# Revit family: NBS_Allermuir_DmstcChrs_Mote-en-us_Sofa
name_source: partatom
category: Furniture
revit_build: Autodesk Revit 2016 (Build: 20151007_0715(x64)
units: mm (PartAtom-declared; Revit-internal decimal feet)

## family parameters
Always vertical = Yes
Cut with Voids When Loaded = No
Room Calculation Point = No
Shared = No
Work Plane-Based = No

## types (17) — shared parameters
AssetType = Moveable
Category = Pr_40_50_12_22:Dining chairs
DurationUnit = year
ExpectedLife = 10
FrameColourOptions = Flint grey, mineral sand, mellow yellow, orange crush
FrameMountingMaterial = NBS_Concept
FramesColour = Black
FramesFinish = Powder coat
FramesMaterial = Aluminum
IfcExportAs = IfcFurnitureType
IfcExportType = SOFA
IsBuiltIn = No
ManufacturerName = Allermuir
ManufacturerURL = http://www.thesenatorgroup.com
NBSCertification = www.nationalbimlibrary.com/cert/or0n0v02
NBSDescription = Domestic chairs
NBSReference = 45-35-20/365
OmniClassCode = 22-12 52 23
OmniClassTitle = Office Seating
OmniClassVersion = Table 22 2012-05-16
ProductInformation = http://www.thesenatorgroup.com
ScreenFinishMaterial = NBS_Concept
SeatArmRestHeight = 24 "
SeatEndRestOffset = 3 "
SeatFrameMaterial = NBS_Concept
SeatFrameWidth = 2 "
SeatLegOffset = 6 "
SeatPowerSupplyMaterial = NBS_Concept
SeatScreenHeight = 52 "
SeatingArmRestMaterial = NBS_Concept
SeatingHeight = 19 "
SeatingSeatMaterial = NBS_Concept
SeatsAndBacksFinish = Two-tone upholstery
SeatsAndBacksMaterial = Upholstered
ShelfMaterial = NBS_Concept
SingleSeatWidth = 39 "
Status = UNSET
ThreeSeatWidth = 87 "
TwoSeatWidth = 63 "
Uniclass2015Code = Pr_40_50_12_22
Uniclass2015Title = Dining chairs
Uniclass2015Version = Products v1.9
Version = 1
WarrantyDescription = Allermuir warrant that its manufactured products are free from manufacturing defects in materials or workmanship for a period of ten years
WarrantyDurationParts = 10
WarrantyDurationUnit = year
zero-valued in all types: HighestSeatingHeight, LowestSeatingHeight

## per-type parameters (varying)
| type | BIMObjectName | Description | Features | HasLeftSideScreen | HasRightSideScreen | HasScreens | HasShelf | IsSingleSeat | IsThreeSeat | IsTwoSeat | LeftSeatPositionOffset | ModelReference | Name | NominalDepth | NominalHeight | NominalLength | NominalWidth | OptionalAccessories | RightSeatPositionWidth | SeatOverallWidth | ShowMultipleSeat | Size |
| MTESF01 | NBS_Allermuir_DomesticChairs_Mote_MTESF01-US | Single seat sofa | Fully upholstered, cast aluminum legs and aluminum perimeter frame finished in black powder coat, plastic glides with leveling adjustment, two-tone upholstery, cast aluminum frame available in flint gray, mineral sand, mellow yellow or orange crush, end arms, 1 x front facing, frame integrated power unit - 2 x powered USB and 1 x power outlet, 1 x rear facing, frame integrated power unit - 2 x powered USB and 1 x power outlet | No | No | No | No | Yes | No | No | 0 " | Mote sofa | DomesticChairs_Mote_MTE-SF01_Allermuir | 39 " | 33 " | 29 " | 39 " | 1 x front facing frame intergrated power unit with 2 x powered USB and 1 x power socket, 1 x rear facing frame intergrated power unit with 2 x powered USB and 1 x power socket, End arms | 16 " | 39 " | No | 28.75 x 39.25 x 32.75" |
| MTESF02 | NBS_Allermuir_DomesticChairs_Mote_MTESF02-US | Two seat sofa | Fully upholstered, cast aluminum legs and aluminum perimeter frame finished in black powder coat, plastic glides with leveling adjustment, end arms, single arm mid, two-tone upholstery, Cast aluminum frame available in flint gray, mineral sand, mellow yellow or orange crush, 1 x front facing, frame integrated power unit - 2 x powered USB and 1 x power outlet, 1 x rear facing, frame integrated power unit - 2 x powered USBand 1 x power outlet | No | No | No | No | No | No | Yes | 0 " | Mote sofa | DomesticChairs_Mote_MTE-SF02_Allermuir | 63 " | 33 " | 29 " | 63 " | 1 x front facing frame intergrated power unit with 2 x powered USB and 1 x power socket, 1x rear facing frame intergrated power unit with 2 x powered USB and 1 x power socket, End arms, Single arm - mid | 16 " | 63 " | Yes | 28.75 x 63 x 32.75" |
| MTESF03 | NBS_Allermuir_DomesticChairs_Mote_MTESF03-US | Three seat sofa | Fully upholstered, cast aluminum legs and aluminum perimeter frame finished in black powder coat, plastic glides with leveling adjustment, end arms,double arms intermediate, two-tone upholstery, 2 x front facing, frame integrated power unit - 2 x powered USB and 1 x power outlet, 2 x rear facing, frame integrated power unit - 2 x powered USB and 1 x power outlet | No | No | No | No | No | Yes | No | 16 " | Mote sofa | DomesticChairs_Mote_MTE-SF03_Allermuir | 87 " | 33 " | 29 " | 87 " | 2 x front facing frame intergrated power unit with 2 x powered USB and 1 x power socket, 2 x rear facing frame intergrated power unit with 2 x powered USB and 1 x power socket, End arms, Double arms - intermediate | 31 " | 87 " | Yes | 28.75 x 86.5 x 32.75" |
| MTEBSS01 | NBS_Allermuir_DomesticChairs_Mote_MTEBSS01-US | Single seat sofa with rear screen | Rear screens, fully upholstered, cast aluminum legs and aluminum perimeter frame finished in black powder coat, plastic glides with leveling adjustment, two-tone upholstery, end arm | No | No | Yes | No | Yes | No | No | 0 " | Mote with rear screen | DomesticChairs_Mote_MTE-BSS01-US_Allermuir | 39 " | 51 " | 29 " | 39 " | End arms, 1 x front facing frame intergrated power unit  2 x powered USB and 1 x power socket, 1 x rear facing frame intergrated power unit  2 x powered USB and 1 x power socket, | 16 " | 39 " | No | 28.75 x 39.25 x 51" |
| MTEBSS02 | NBS_Allermuir_DomesticChairs_Mote_MTEBSS02-US | Two seat sofa with rear screen | Rear screens, fully upholstered, cast aluminum legs and aluminum perimeter frame finished in black powder coat, plastic glides with leveling adjustment, end arms, single arm mid, two-tone upholstery, end arms, Single arm - mid | No | No | Yes | No | No | No | Yes | 0 " | Mote with rear screen | DomesticChairs_Mote_MTE-BSS02-US_Allermuir | 63 " | 51 " | 29 " | 63 " | End arms, Single arm - mid, 1 x front facing, frame intergrated power unit  2 x powered USB and 1 x power socket, 1 x rear facing, frame intergrated power unit  2 x powered USB and 1 x power socket, | 16 " | 63 " | Yes | 28.75 x 63 x 51" |
| MTEBSS03 | NBS_Allermuir_DomesticChairs_Mote_MTEBSS03-US | Three seat sofa with rear screen | Rear screens, fully Upholstered, cast aluminum legs and aluminum perimeter frame finished in black powder coat, plastic glides with leveling adjustment, end arms, double arms intermediate, two-tone upholstery, end arms, double arms - intermediate | No | No | Yes | No | No | Yes | No | 16 " | Mote with rear screen | DomesticChairs_Mote_MTE-BSS03-US_Allermuir | 87 " | 51 " | 29 " | 87 " | End arms, Double arms - intermediate, 2 x front facing frame intergrated power unit with 2 x powered USB and 1 x power socket, 2 x rear facing frame intergrated power unit with 2 x powered USB and 1 x power socket | 31 " | 87 " | Yes | 28.75 x 86.5 x 51" |
| MTEBSF01 | NBS_Allermuir_DomesticChairs_Mote_MTEBSF01-US | Single seat sofa with rear and side screens | Rear and side screens, Fully Upholstered, End arms, Cast aluminum legs and aluminum perimeter frame finished in black powder coat, Plastic glides with leveling adjustment, Aluminum frame available in flint grey, mineral sand, mellow yellow or orange crush powder coat, 4x bag/coat hooks finished in satin chrome fitted to left and right hand outer screens, 1x front facing, frame intergrated power unit - 2 x powered USB and 1 x power socket, 1x rear facing, frame intergrated power unit - 2 x powered USB and 1 x power socket, two-tone upholstery | Yes | Yes | Yes | No | Yes | No | No | 0 " | Mote with side and rear screen | DomesticChairs_Mote_MTE-BSF01-US_Allermuir | 43 " | 52 " | 31 " | 43 " | Rear and side screens, fully upholstered, end arms, cast aluminum legs and aluminum perimeter frame finished in black powder coat, plastic glides with leveling adjustment, aluminum frame available in flint grey, mineral sand, mellow yellow or orange crush powder coat, 4 x bag/coat hooks finished in satin chrome fitted to left and right hand outer screens, 1 x front facing, frame intergrated power unit  2 x powered USB and 1 x power socket, 1 x rear facing, frame intergrated power unit 2 x powered USB and 1 x power socket, two-tone upholstery | 16 " | 39 " | No | 30.5 x 43 x 51.5" |
| MTEBSF02 | NBS_Allermuir_DomesticChairs_Mote_MTEBSF02-US | Two seat sofa with rear and side screens | Rear and side screens, Fully Upholstered, End arms, Cast aluminum legs and aluminum perimeter frame finished in black powder coat, Plastic glides with leveling adjustment, Aluminum frame available in flint grey, mineral sand, mellow yellow or orange crush powder coat, single arm - mid, 4x bag/coat hooks finished in satin chrome fitted to left and right hand outer screens, 1x front facing, frame intergrated power unit - 2 x powered USB and 1 x power socket, 1x rear facing, frame intergrated power unit - 2 x powered USB and 1 x power socket, two-tone upholstery | Yes | Yes | Yes | No | No | No | Yes | 0 " | Mote with side and rear screen | DomesticChairs_Mote_MTE-BSF02-US_Allermuir | 67 " | 52 " | 31 " | 67 " | Rear and side screens, fully upholstered, end arms, cast aluminum legs and aluminum perimeter frame finished in black powder coat, plastic glides with leveling adjustment, aluminum frame available in flint grey, mineral sand, mellow yellow or orange crush powder coat, single arm mid, 4 x bag/coat hooks finished in satin chrome fitted to left and right hand outer screens, 1 x front facing, frame intergrated power unit 2 x powered USB and 1 x power socket, 1 x rear facing, frame intergrated power unit 2 x powered USB and 1 x power socket, two-tone upholstery | 16 " | 63 " | Yes | 30.5 x 66.5 x 51.5" |
| MTEBSF03 | NBS_Allermuir_DomesticChairs_Mote_MTEBSF03-US | Three seat sofa with rear and side screens | Rear and side screens, Fully Upholstered, End arms, Cast aluminum legs and aluminum perimeter frame finished in black powder coat, Plastic glides with leveling adjustment, Aluminum frame available in flint grey, mineral sand, mellow yellow or orange crush powder coat, double arms - intermediate, 4x bag/coat hooks finished in satin chrome fitted to left and right hand outer screens, 2x front facing, frame intergrated power unit - 2 x powered USB and 1 x power socket, 2x rear facing, frame intergrated power unit - 2 x powered USB and 1 x power socket, two-tone upholstery | Yes | Yes | Yes | No | No | Yes | No | 16 " | Mote with side and rear screen | DomesticChairs_Mote_MTE-BSF03-US_Allermuir | 90 " | 52 " | 31 " | 90 " | Rear and side screens, fully upholstered, end arms, cast aluminum legs and aluminum perimeter frame finished in black powder coat, plastic glides with leveling adjustment, aluminum frame available in flint grey, mineral sand, mellow yellow or orange crush powder coat, double arms - intermediate, 4 x bag/coat hooks finished in satin chrome fitted to left and right hand outer screens, 2 x front facing, frame intergrated power unit - 2 x powered USB and 1 x power socket, 2 x rear facing, frame intergrated power unit 2 x powered USB and 1 x power socket, two-tone upholstery | 31 " | 87 " | Yes | 30.5 x 90.25 x 51.5" |
| MTEBCSL01 | NBS_Allermuir_DomesticChairs_Mote_MTEBCSL01-US | Single seat sofa with rear and left hand corner screen | Rear and left hand corner screen with arm, Fully Upholstered, Cast aluminum legs and aluminum perimeter frame finished in black powder coat, Plastic glides with leveling adjustment, Aluminum frame available in flint grey, mineral sand, mellow yellow or orange crush powder coat, 2x bag/coat hooks finished in satin chrome fitted to the outer left hand screen, 1x front facing, frame intergrated power unit - 2 x powered USB and 1 x power socket, 2x rear facing, frame intergrated power unit - 2 x powered USB and 1 x power socket, two-tone upholstery | Yes | No | Yes | No | Yes | No | No | 0 " | Mote with side and rear screen | DomesticChairs_Mote_MTE-BCSL01-US_Allermuir | 41 " | 52 " | 31 " | 41 " | Rear and left hand corner screen with arm, fully upholstered, cast aluminum legs and aluminum perimeter frame finished in black powder coat, plastic glides with leveling adjustment, aluminum frame available in flint grey, mineral sand, mellow yellow or orange crush powder coat, 2 x bag/coat hooks finished in satin chrome fitted to the outer left hand screen, 1 x front facing, frame intergrated power unit 2 x powered USB and 1 x power socket, 2 x rear facing, frame intergrated power unit 2 x powered USB and 1 x power socket, two-tone upholstery | 16 " | 39 " | No | 305. x 41.25 x 51.5" |
| MTEBCSR01 | NBS_Allermuir_DomesticChairs_Mote_MTEBCSR01-US | Single seat sofa with rear and right hand corner screen | Rear and right hand corner screen with arm, Fully Upholstered, Cast aluminum legs and aluminum perimeter frame finished in black powder coat, Plastic glides with leveling adjustment, Aluminum frame available in flint grey, mineral sand, mellow yellow or orange crush powder coat, 2x bag/coat hooks finished in satin chrome fitted to the outer right hand screen, 1x front facing, frame intergrated power unit - 2 x powered USB and 1 x power socket, 2x rear facing, frame intergrated power unit - 2 x powered USB and 1 x power socket, two-tone upholstery | No | Yes | Yes | No | Yes | No | No | 0 " | Mote with side and rear screen | DomesticChairs_Mote_MTE-BCSR01-US_Allermuir | 41 " | 52 " | 31 " | 41 " | Rear and right hand corner screen with arm, fully upholstered, cast aluminum legs and aluminum perimeter frame finished in black powder coat, plastic glides with leveling adjustment, aluminum frame available in flint grey, mineral sand, mellow yellow or orange crush powder coat, 2 x bag/coat hooks finished in satin chrome fitted to the outer right hand screen, 1 x front facing, frame intergrated power unit 2 x powered USB and 1 x power socket, 2 x rear facing, frame intergrated power unit 2 x powered USB and 1 x power socket, two-tone upholstery | 16 " | 39 " | No | 30.5 x 41.25 x 51.5" |
| MTEBSS01T | NBS_Allermuir_DomesticChairs_Mote_MTEBSS01T-US | Single seat sofa with rear screen and work shelf | 1" white TRL rear mounted work shelf with a clear edge profile and scallop cut out (edge ref 44), rear screens, fully upholstered, cast aluminum legs and aluminum perimeter frame finished in black powder coat, plastic glides with leveling adjustment, rear mounted work shelf available in all standard TFL finishes, work shelf edge profile can be stained, end arms | No | No | Yes | Yes | Yes | No | No | 0 " | Mote with work shelf | DomesticChairs_Mote_MTE-BSS01T-US_Allermuir | 39 " | 52 " | 43 " | 39 " | End arms, 1 x front facing, frame integrated power unit 2 x powered USB and 1 x power socket, 1 x rear facing, frame integrated power unit 2 x powered USB and 1 x power socket, two-tone upholstery | 16 " | 39 " | No | 42.5 x 39.25 x 51.5" |
| MTEBSS02T | NBS_Allermuir_DomesticChairs_Mote_MTEBSS02T-US | Two seat sofa with rear screen and work shelf | 1" white TFL rear mounted work shelf with a clear edge profile and scallop cut out (edge ref 44), rear screens, fully upholstered, cast aluminum legs and aluminum perimeter frame finished in black powder coat, plastic glides with leveling adjustment, rear mounted work shelf available in all standard TFL finishes, work shelf edge profile can be stained, end arms, single arm - mid | No | No | Yes | Yes | No | No | Yes | 0 " | Mote with work shelf | DomesticChairs_Mote_MTE-BSS02T-US_Allermuir | 63 " | 52 " | 43 " | 63 " | End arms, singe arm - mid, 1 x front facing, frame integrated power unit 2 x powered USB and 1 x power socket, 1 x rear facing, frame integrated power unit 2 x powered USB and 1 x power socket, two-tone upholstery | 16 " | 63 " | Yes | 42.5 x 63 x 51.5" |
| MTEBSS03T | NBS_Allermuir_DomesticChairs_Mote_MTEBSS03T-US | Three seat sofa with rear screen and work shelf | 1" white TFL rear mounted work shelf with a clear edge profile and scallop cut out (edge ref 44), rear screens, fully upholstered, cast aluminum legs and aluminum perimeter frame finished in black powder coat, plastic glides with leveling adjustment, rear mounted work shelf available in all standard TFL finishes, work shelf edge profile can be stained, end arms, double arms - intermediate | No | No | Yes | Yes | No | Yes | No | 16 " | Mote with work shelf | DomesticChairs_Mote_MTE-BSS03T-US_Allermuir | 87 " | 52 " | 43 " | 87 " | End arms, Double arms - intermediate, 1 x front facing, frame integrated power unit 2 x powered USB and 1 x power socket, 1 x rear facing, frame integrated power unit 2 x powered USB and 1 x power socket, two-tone upholstery | 31 " | 87 " | Yes | 42.5 x 86.5 x 51.5" |
| MTEBSF01T | NBS_Allermuir_DomesticChairs_Mote_MTEBSF01T-US | Single seat sofa with rear and side screens and work shelf | 1" white TFL rear mounted work shelf with a clear edge profile and scallop cut out (edge ref 44), rear and side screens, fully upholstered, end arms, cast aluminum legs and aluminum perimeter frame finished in black powder coat, plastic glides with leveling adjustment, rear mounted work shelf available in all standard TFL finishes, work shelf edge profile can be stained | Yes | Yes | Yes | Yes | Yes | No | No | 0 " | Mote with work shelf | DomesticChairs_Mote_MTE-BSF01T-US_Allermuir | 43 " | 52 " | 43 " | 43 " | 4 x bag coat hooks finished in satin chrome fitted to left and right hand outer screens, 1 x front facing, frame integrated power unit 2 x powered USB and 1 x power socket, 1 x rear facing, frame integrated power unit 2 x powered USB and 1 x power socket, two-tone upholstery | 16 " | 39 " | No | 42.5 x 51.5 x 43" |
| MTEBSF02T | NBS_Allermuir_DomesticChairs_Mote_MTEBSF02T-US | Two seat sofa with rear and side screens and work shelf | 1" white TFL rear mounted work shelf with a clear edge profile and scallop cut out (edge ref 44), rear and side screens, fully upholstered, end arms, cast aluminum legs and aluminum perimeter frame finished in black powder coat, plastic glides with leveling adjustment, rear mounted work shelf available in all standard TFL finishes, work shelf edge profile can be stained, single arm mid | Yes | Yes | Yes | Yes | No | No | Yes | 0 " | Mote with work shelf | DomesticChairs_Mote_MTE-BSF02T-US_Allermuir | 67 " | 52 " | 43 " | 67 " | Singe arm - mid, 4 x bag coat hooks finished in satin chrome fitted to left and right hand outer screens, 1 x front facing, frame integrated power unit 2 x powered USB and 1 x power socket, 1 x rear facing, frame integrated power unit 2 x powered USB and 1 x power socket, two-tone upholstery | 16 " | 63 " | Yes | 42.5 x 66.5 x 51.5" |
| MTEBSF03T | NBS_Allermuir_DomesticChairs_Mote_MTEBSF03T-US | Three seat sofa with rear and side screens and work shelf | 1" white TFL rear mounted work shelf with a clear edge profile and scallop cut out (edge ref 44), rear and side screens, fully upholstered, end arms, cast aluminum legs and aluminum perimeter frame finished in black powder coat, plastic glides with leveling adjustment, rear mounted work shelf available in all standard TFL finishes, work shelf edge profile can be stained, double arms intermediate | Yes | Yes | Yes | Yes | No | Yes | No | 16 " | Mote with work shelf | DomesticChairs_Mote_MTE-BSF03T-US_Allermuir | 90 " | 52 " | 43 " | 90 " | Double arms - intermediate, 4 x bag coat hooks finished in satin chrome fitted to left and right hand outer screens, 2 x front facing, frame integrated power unit 2 x powered USB and 1 x power socket, 2 x rear facing, frame integrated power unit 2 x powered USB and 1 x power socket, two-tone upholstery | 31 " | 87 " | Yes | 42.5 x 90.25 x 51.5" |

note: column(s) folded — value = type name in every type: ModelNumber

## geometry (parser evidence)
native form markers: Sweep x13
no freeform markers — native parametric forms only
